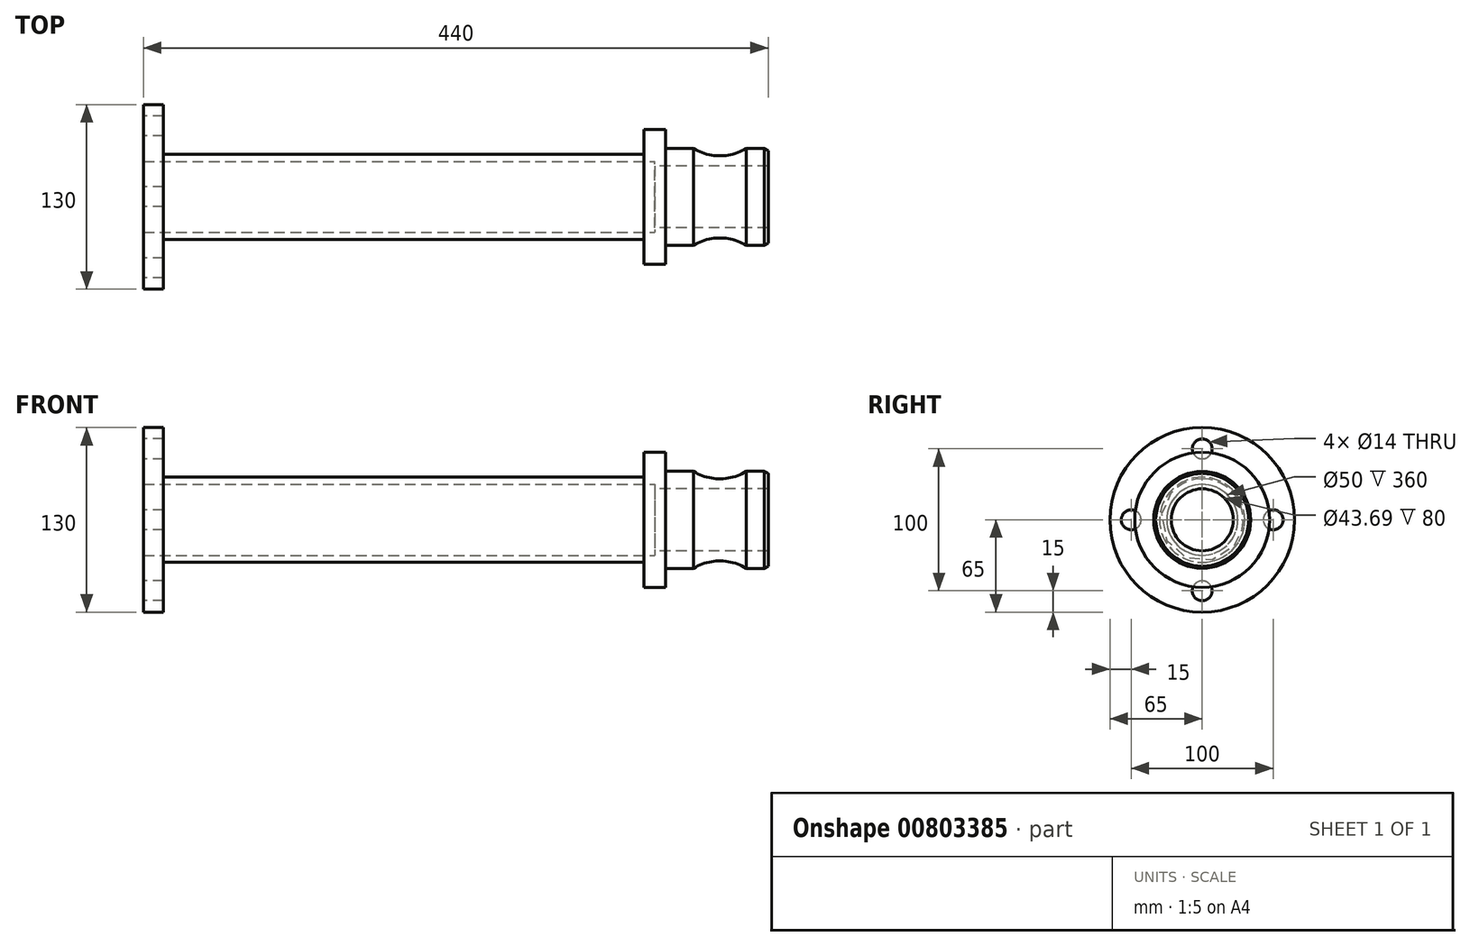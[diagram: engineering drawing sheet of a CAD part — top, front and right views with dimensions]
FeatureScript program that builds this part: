
annotation { "Feature Type Name" : "Feature", "Feature Type Description" : "" }
export const myFeature = defineFeature(function(context is Context, id is Id, definition is map)
    precondition{}
    {
        {
            var Q0;
            Q0=qCreatedBy(makeId("Top.planeOp"),FACE);
            var sketch = newSketch(context, id + "F0", { "sketchPlane" : qUnion([Q0])});
            skLineSegment(sketch, "E0", {"start": v(0, 0) * mm, "end": v(360, 0) * mm});
            skPoint(sketch, "E1.visualSharp", {"position": v(250, 0) * mm});
            skSolve(sketch);
        }
        {
            var Q0;
            Q0=qCreatedBy(makeId("Right.planeOp"),FACE);
            var sketch = newSketch(context, id + "F1", { "sketchPlane" : qUnion([Q0])});
            skCircle(sketch, "E2", {"center": v(0, 0) * mm, "radius": 25 * mm});
            skCircle(sketch, "E3", {"center": v(0, 0) * mm, "radius": 30 * mm});
            skSolve(sketch);
        }
        {
            var Q0;
            Q0=makeQuery(id+"F1.imprint","IMPRINT",FACE,{"disambiguationData":[TD([[makeQuery(id+"F1.imprint","IMPRINT",EDGE,{"derivedFrom":sQuery(id+"F1.wireOp",EDGE,"E2")}),-1.0]])]});
            var Q1;
            Q1=sQuery(id+"F0.wireOp",EDGE,"E0");
            var Q2;
            Q2=sQuery(id+"F0.wireOp",EDGE,"E1.filletArc");
            var Q3;
            Q3=sQuery(id+"F0.wireOp",EDGE,"vY9ck2b2-czU3-8NDb-ky81-hxEUZ02ooPQc");
            sweep(context, id + "F2", {"profiles" : qUnion([Q0]), "path" : qUnion([Q1, Q2, Q3])});
        }
        {
            var Q0;
            Q0=qCreatedBy(makeId("Right.planeOp"),FACE);
            var sketch = newSketch(context, id + "F3", { "sketchPlane" : qUnion([Q0])});
            skCircle(sketch, "E4", {"center": v(0, 0) * mm, "radius": 65 * mm});
            skCircle(sketch, "E5", {"center": v(0, 50) * mm, "radius": 7 * mm});
            skCircle(sketch, "E6.1.0", {"center": v(-50, 0) * mm, "radius": 7 * mm});
            skCircle(sketch, "E6.2.0", {"center": v(0, -50) * mm, "radius": 7 * mm});
            skCircle(sketch, "E6.3.0", {"center": v(50, 0) * mm, "radius": 7 * mm});
            skCircle(sketch, "E7.0", {"center": v(0, 0) * mm, "radius": 25 * mm});
            skSolve(sketch);
        }
        {
            var Q0;
            Q0 = qSketchRegion(id + "F3", true);
            extrude(context, id + "F4", {"entities" : qUnion([Q0]), "operationType" : NewBodyOperationType.ADD, "depth" : 14 * mm, "offsetDistance" : 25 * mm});
        }
        {
            var Q0;
            Q0=qCreatedBy(makeId("Front.planeOp"),FACE);
            var sketch = newSketch(context, id + "F5", { "sketchPlane" : qUnion([Q0])});
            skLineSegment(sketch, "E8.0", {"start": v(360, -21.85) * mm, "end": v(360, -30) * mm});
            skLineSegment(sketch, "E9.top", {"start": v(367.5, -47.5) * mm, "end": v(352.5, -47.5) * mm});
            skLineSegment(sketch, "E9.left", {"start": v(367.5, -34.16) * mm, "end": v(367.5, -47.5) * mm});
            skPoint(sketch, "E9.middle", {"position": v(360, 0) * mm});
            skLineSegment(sketch, "E10", {"start": v(367.5, -34.16) * mm, "end": v(387.33, -34.16) * mm});
            skArc(sketch, "E11", {"start": v(424.44, -34.16) * mm, "mid": v(405.89, -28.9) * mm, "end": v(387.33, -34.16) * mm});
            skLineSegment(sketch, "E12", {"start": v(424.44, -34.16) * mm, "end": v(437.04, -34.16) * mm});
            skLineSegment(sketch, "E13", {"start": v(437.04, -34.16) * mm, "end": v(440, -32.67) * mm});
            skLineSegment(sketch, "E14", {"start": v(440, -32.67) * mm, "end": v(440, -21.85) * mm});
            skLineSegment(sketch, "E15", {"start": v(440, -21.85) * mm, "end": v(367.5, -21.85) * mm});
            skLineSegment(sketch, "E16", {"start": v(367.5, -21.85) * mm, "end": v(352.5, -21.85) * mm});
            skLineSegment(sketch, "E17.trimOffspring", {"start": v(352.5, -21.85) * mm, "end": v(352.5, -47.5) * mm});
            skPoint(sketch, "E9.bottom.end.orphan", {"position": v(352.5, 47.5) * mm});
            skPoint(sketch, "E9.bottom.start.orphan", {"position": v(367.5, 47.5) * mm});
            skPoint(sketch, "E18.orphan", {"position": v(360, 30) * mm});
            skLineSegment(sketch, "E19.trimOffspring", {"start": v(360, -30) * mm, "end": v(124, -30) * mm});
            skSolve(sketch);
        }
        {
            var Q0;
            {var subQ1=sQuery(id+"F5.wireOp",EDGE,"E8.0");Q0=makeQuery(id+"F5.imprint","IMPRINT",FACE,{"disambiguationData":[TD([[makeQuery(id+"F5.imprint","IMPRINT",EDGE,{"derivedFrom":subQ1}),1.0]])]});}
            var Q1;
            Q1=makeQuery(id+"F2.opSweep","SWEPT_FACE",FACE,{"disambiguationData":[OSD([sQuery(id+"F0.wireOp",EDGE,"E0"),sQuery(id+"F1.wireOp",EDGE,"E3")])]});
            revolve(context, id + "F6", {"operationType" : NewBodyOperationType.ADD, "surfaceOperationType" : NewSurfaceOperationType.NEW, "entities" : qUnion([Q0]), "axis" : qUnion([Q1]), "revolveType" : RevolveType.FULL});
        }
    });
